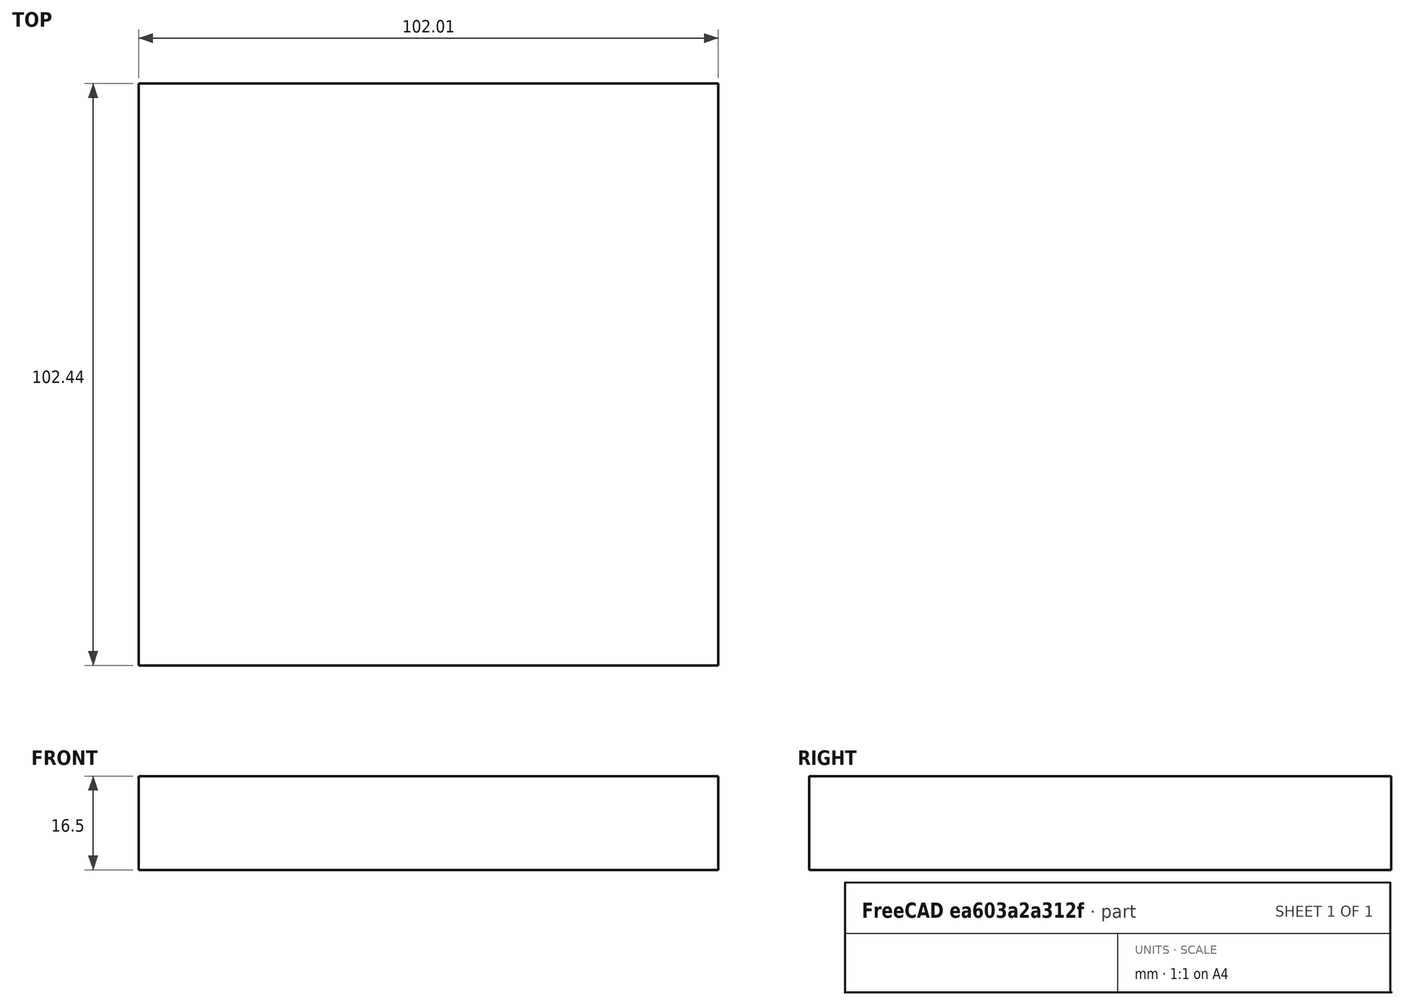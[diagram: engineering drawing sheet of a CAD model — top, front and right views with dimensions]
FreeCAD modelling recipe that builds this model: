
FCSTD DOCUMENT  (FreeCAD 1.0R39319 (Git))
Label: CableManagement
License: All rights reserved
LicenseURL: https://en.wikipedia.org/wiki/All_rights_reserved
objects: Sketcher::SketchObject×2, PartDesign::Body×2, PartDesign::Pad×1
note: 9 computed .brp shape members not serialized (recipe doc carries the construction recipe); baked Part::Feature solids carry a one-line shape summary decoded from their .brp

FEATURE [Sketcher::SketchObject] Sketch
  ArcFitTolerance = 1e-06
  AttachmentSupport = -> [XY_Plane]
  FullyConstrained = false
  MakeInternals = false
  MapMode = 5
  sketch-geometry (4):
    g0: LineSegment StartX=0 StartY=0 StartZ=0 EndX=102.011 EndY=0 EndZ=0
    g1: LineSegment StartX=102.011 StartY=0 StartZ=0 EndX=102.011 EndY=102.443 EndZ=0
    g2: LineSegment StartX=102.011 StartY=102.443 StartZ=0 EndX=0 EndY=102.443 EndZ=0
    g3: LineSegment StartX=0 StartY=102.443 StartZ=0 EndX=0 EndY=0 EndZ=0
  constraints (9):
    c: Coincident(g0,g1)
    c: Coincident(g1,g2)
    c: Coincident(g2,g3)
    c: Coincident(g3,g0)
    c: Horizontal(g0)
    c: Horizontal(g2)
    c: Vertical(g1)
    c: Vertical(g3)
    c: Coincident(g0,g-1)
FEATURE [PartDesign::Pad] Pad
  Direction = (0,0,1)
  Length = 16.5
  Length2 = 10
  Profile = -> Sketch
  ReferenceAxis = -> Sketch [N_Axis]
  Refine = true
  Suppressed = false
  Type = 0
FEATURE [PartDesign::Body] Body
  AllowCompound = false
  Group = -> [Sketch,Pad]
  Origin = -> Origin
  Tip = -> Pad
FEATURE [Sketcher::SketchObject] Sketch001
  ArcFitTolerance = 1e-06
  AttachmentSupport = -> [XZ_Plane001]
  FullyConstrained = false
  MakeInternals = false
  MapMode = 5
  Placement = pos=(0,0,0) rot=(1,0,0;1.5708rad)
  sketch-geometry (4):
    g0: LineSegment StartX=5.03329 StartY=20.7878 StartZ=0 EndX=5.03329 EndY=-5.71223 EndZ=0
    g1: LineSegment StartX=5.03329 StartY=-5.71223 StartZ=0 EndX=31.5333 EndY=-5.71223 EndZ=0
    g2: LineSegment StartX=31.5333 StartY=-5.71223 StartZ=0 EndX=31.5333 EndY=20.7878 EndZ=0
    g3: LineSegment StartX=31.5333 StartY=20.7878 StartZ=0 EndX=5.03329 EndY=20.7878 EndZ=0
  constraints (10):
    c: Coincident(g0,g1)
    c: Coincident(g1,g2)
    c: Coincident(g2,g3)
    c: Coincident(g3,g0)
    c: Vertical(g0)
    c: Vertical(g2)
    c: Horizontal(g1)
    c: Horizontal(g3)
    c: Distance(g3,g3) = 26.5
    c: Distance(g0,g0) = 26.5
FEATURE [PartDesign::Body] Body001
  AllowCompound = false
  Group = -> [Sketch001]
  Origin = -> Origin001
